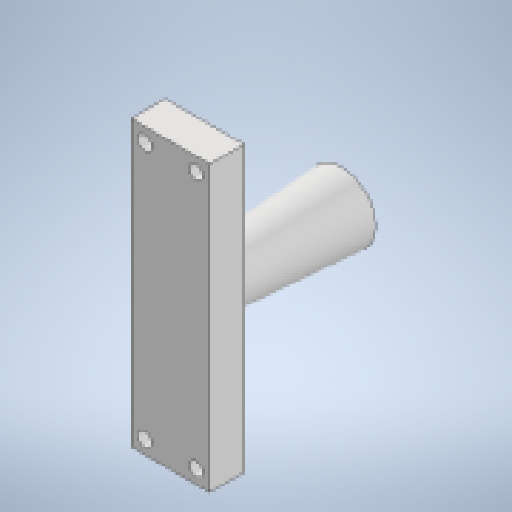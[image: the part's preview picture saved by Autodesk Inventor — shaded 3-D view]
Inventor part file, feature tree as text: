
AUTODESK INVENTOR PART (.ipt)
format: ipt  version: 2024 (Build 280153000, 153)  size: 178,688 bytes
history: native  units: mm
features: other x4, sketch x4, plane x3, extrude x2, reference x2, loft x1
ambient origin geometry x8: Origin, YZ Plane, XZ Plane, XY Plane, X Axis, Y Axis, Z Axis, Center Point
bodies: Body1 (feature_tree)
feature tree (16):
  other  "Sólido1"
  sketch  "Boceto1"  dims[d18=15.0mm d19=75.0mm]
  plane  "Plano de trabajo2"
  plane  "Plano de trabajo5"
  extrude  "Extrusión5"  Depth=75.0mm
  plane  "Plano de trabajo4"
  loft  "Solevación1"
  extrude  "Extrusión6"  TaperAngle=0.0deg  [1 undecoded]
  reference  "Referencia1"
  reference  "Referencia2"
  sketch  "Boceto7"  dims[d20=10.0mm d21=0.0mm d22=15.0mm]
  sketch  "Boceto9"  dims[d23=10.0mm d24=0.0mm d25=90.0deg]
  sketch  "Boceto10"  dims[d26=0.0mm d27=90.0deg d28=0.0mm d30=8.0mm d31=0.0mm d32=23.0mm d33=83.0mm d35=7.5mm d36=4.044mm d37=4.044mm]
  other  "ENSAMBLAJE_VENTOSA_2.iam"
  other  "ACOPLE:1"
  other  "VENTOSA_B:2"
note: 1 required parameter value undecoded (feature->parameter linkage not recoverable at this tier; creation-order binding heuristic only, values carry confidence <= 0.55)
